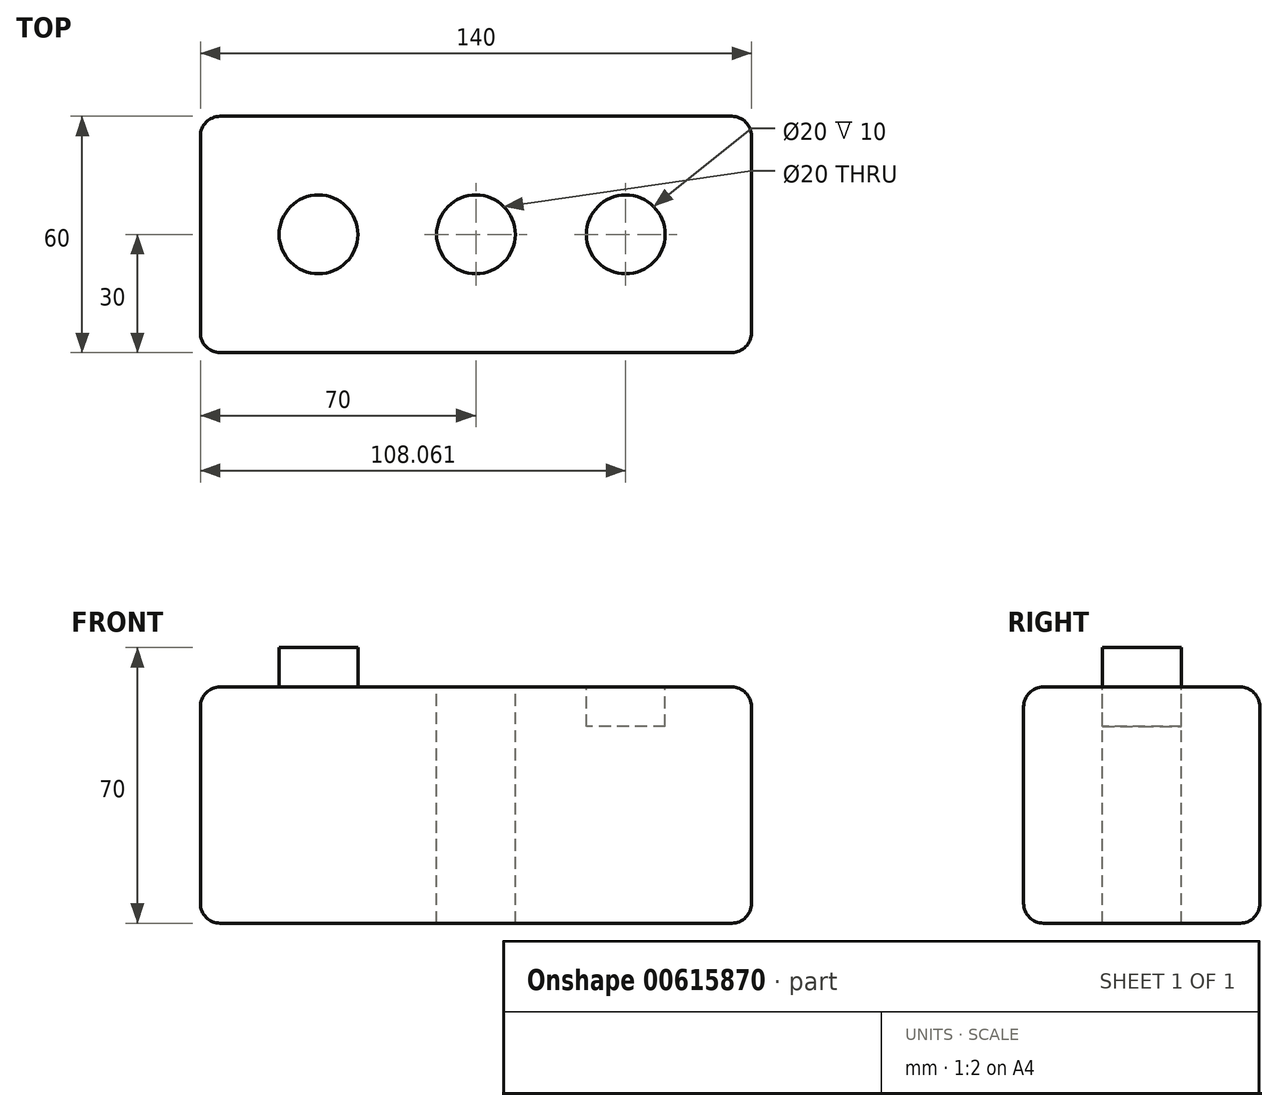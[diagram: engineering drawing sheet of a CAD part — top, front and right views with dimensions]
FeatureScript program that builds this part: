
annotation { "Feature Type Name" : "Feature", "Feature Type Description" : "" }
export const myFeature = defineFeature(function(context is Context, id is Id, definition is map)
    precondition{}
    {
        {
            var Q0;
            Q0=qCreatedBy(makeId("Top.planeOp"),FACE);
            var sketch = newSketch(context, id + "F0", { "sketchPlane" : qUnion([Q0])});
            skLineSegment(sketch, "E0.bottom", {"start": v(-70, 30) * mm, "end": v(70, 30) * mm});
            skLineSegment(sketch, "E0.top", {"start": v(-70, -30) * mm, "end": v(70, -30) * mm});
            skLineSegment(sketch, "E0.left", {"start": v(-70, 30) * mm, "end": v(-70, -30) * mm});
            skLineSegment(sketch, "E0.right", {"start": v(70, 30) * mm, "end": v(70, -30) * mm});
            skPoint(sketch, "E0.middle", {"position": v(0, 0) * mm});
            skSolve(sketch);
        }
        {
            var Q0;
            Q0 = qSketchRegion(id + "F0", true);
            extrude(context, id + "F1", {"entities" : qUnion([Q0]), "depth" : 60 * mm, "offsetDistance" : 25 * mm});
        }
        {
            var Q0;
            Q0=makeQuery(id+"F1.opExtrude","CAP_FACE",FACE,{"disambiguationData":[OSD([sQuery(id+"F0.wireOp",EDGE,"E0.bottom"),sQuery(id+"F0.wireOp",EDGE,"E0.top"),sQuery(id+"F0.wireOp",EDGE,"E0.left"),sQuery(id+"F0.wireOp",EDGE,"E0.right")])],"isStart":false});
            var sketch = newSketch(context, id + "F2", { "sketchPlane" : qUnion([Q0])});
            skCircle(sketch, "E1", {"center": v(-40, 0) * mm, "radius": 10 * mm});
            skSolve(sketch);
        }
        {
            var Q0;
            Q0=makeQuery(id+"F2.imprint","IMPRINT",FACE,{"disambiguationData":[TD([[makeQuery(id+"F2.imprint","IMPRINT",EDGE,{"derivedFrom":sQuery(id+"F2.wireOp",EDGE,"E1")}),-1.0]])]});
            var sketch = newSketch(context, id + "F3", { "sketchPlane" : qUnion([Q0])});
            skCircle(sketch, "E2", {"center": v(38.06, 0) * mm, "radius": 10 * mm});
            skSolve(sketch);
        }
        {
            var Q0;
            Q0=makeQuery(id+"F2.imprint","IMPRINT",FACE,{"disambiguationData":[TD([[makeQuery(id+"F2.imprint","IMPRINT",EDGE,{"derivedFrom":sQuery(id+"F2.wireOp",EDGE,"E1")}),-1.0]])]});
            var sketch = newSketch(context, id + "F4", { "sketchPlane" : qUnion([Q0])});
            skCircle(sketch, "E3", {"center": v(0, 0) * mm, "radius": 10 * mm});
            skSolve(sketch);
        }
        {
            var Q0;
            Q0 = qSketchRegion(id + "F2", true);
            extrude(context, id + "F5", {"entities" : qUnion([Q0]), "operationType" : NewBodyOperationType.ADD, "depth" : 10 * mm, "offsetDistance" : 25 * mm});
        }
        {
            var Q0;
            Q0 = qSketchRegion(id + "F3", true);
            extrude(context, id + "F6", {"entities" : qUnion([Q0]), "operationType" : NewBodyOperationType.REMOVE, "oppositeDirection" : true, "depth" : 10 * mm, "offsetDistance" : 25 * mm});
        }
        {
            var Q0;
            Q0 = qSketchRegion(id + "F4", true);
            extrude(context, id + "F7", {"entities" : qUnion([Q0]), "operationType" : NewBodyOperationType.REMOVE, "oppositeDirection" : true, "depth" : 877 * mm, "offsetDistance" : 25 * mm});
        }
        {
            var Q0;
            Q0=makeQuery(id+"F1.opExtrude","CAP_EDGE",EDGE,{"disambiguationData":[OSD([sQuery(id+"F0.wireOp",EDGE,"E0.top")])],"isStart":false});
            var Q1;
            Q1=makeQuery(id+"F1.opExtrude","CAP_EDGE",EDGE,{"disambiguationData":[OSD([sQuery(id+"F0.wireOp",EDGE,"E0.bottom")])],"isStart":false});
            var Q2;
            Q2=makeQuery(id+"F1.opExtrude","CAP_EDGE",EDGE,{"disambiguationData":[OSD([sQuery(id+"F0.wireOp",EDGE,"E0.left")])],"isStart":false});
            var Q3;
            Q3=makeQuery(id+"F1.opExtrude","CAP_EDGE",EDGE,{"disambiguationData":[OSD([sQuery(id+"F0.wireOp",EDGE,"E0.right")])],"isStart":false});
            var Q4;
            Q4=makeQuery(id+"F1.opExtrude","SWEPT_EDGE",EDGE,{"disambiguationData":[OSD([sQuery(id+"F0.wireOp",EDGE,"E0.top"),sQuery(id+"F0.wireOp",EDGE,"E0.left")])]});
            var Q5;
            Q5=makeQuery(id+"F1.opExtrude","SWEPT_EDGE",EDGE,{"disambiguationData":[OSD([sQuery(id+"F0.wireOp",EDGE,"E0.bottom"),sQuery(id+"F0.wireOp",EDGE,"E0.left")])]});
            var Q6;
            Q6=makeQuery(id+"F1.opExtrude","CAP_EDGE",EDGE,{"disambiguationData":[OSD([sQuery(id+"F0.wireOp",EDGE,"E0.left")])],"isStart":true});
            var Q7;
            Q7=makeQuery(id+"F1.opExtrude","SWEPT_EDGE",EDGE,{"disambiguationData":[OSD([sQuery(id+"F0.wireOp",EDGE,"E0.top"),sQuery(id+"F0.wireOp",EDGE,"E0.right")])]});
            var Q8;
            Q8=makeQuery(id+"F1.opExtrude","CAP_EDGE",EDGE,{"disambiguationData":[OSD([sQuery(id+"F0.wireOp",EDGE,"E0.right")])],"isStart":true});
            var Q9;
            Q9=makeQuery(id+"F1.opExtrude","SWEPT_EDGE",EDGE,{"disambiguationData":[OSD([sQuery(id+"F0.wireOp",EDGE,"E0.bottom"),sQuery(id+"F0.wireOp",EDGE,"E0.right")])]});
            var Q10;
            Q10=makeQuery(id+"F1.opExtrude","CAP_EDGE",EDGE,{"disambiguationData":[OSD([sQuery(id+"F0.wireOp",EDGE,"E0.top")])],"isStart":true});
            var Q11;
            Q11=makeQuery(id+"F1.opExtrude","CAP_EDGE",EDGE,{"disambiguationData":[OSD([sQuery(id+"F0.wireOp",EDGE,"E0.bottom")])],"isStart":true});
            fillet(context, id + "F8", {"entities" : qUnion([Q0, Q1, Q2, Q3, Q4, Q5, Q6, Q7, Q8, Q9, Q10, Q11]), "radius" : 5 * mm, "tangentPropagation" : true, "allowEdgeOverflow" : false});
        }
    });
